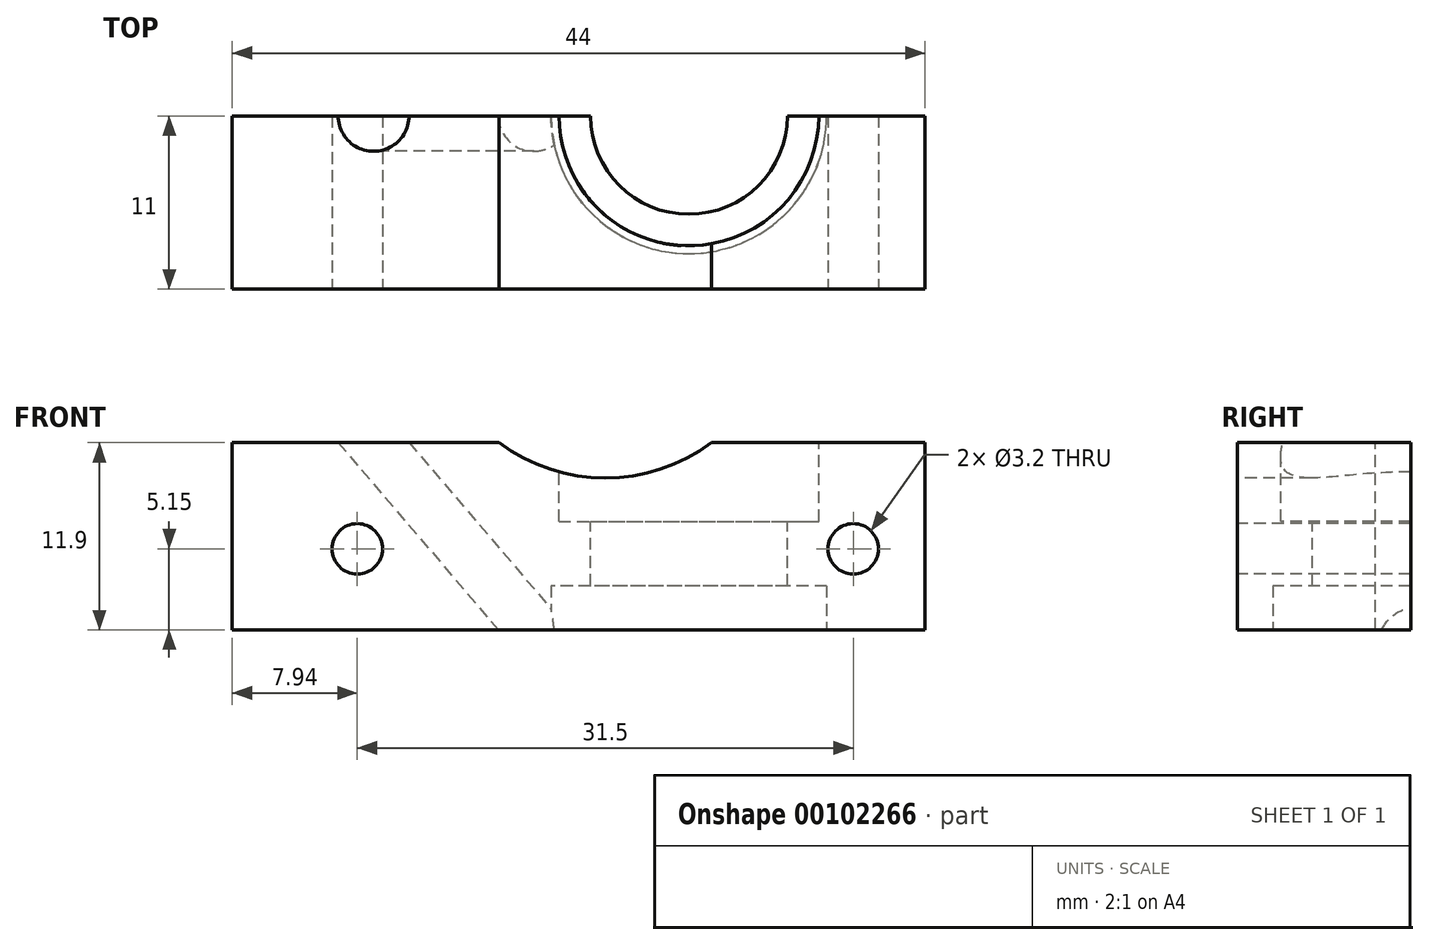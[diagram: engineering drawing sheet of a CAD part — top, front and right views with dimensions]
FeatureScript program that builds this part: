
annotation { "Feature Type Name" : "Feature", "Feature Type Description" : "" }
export const myFeature = defineFeature(function(context is Context, id is Id, definition is map)
    precondition{}
    {
        {
            var Q0;
            Q0=qCreatedBy(makeId("Top.planeOp"),FACE);
            var sketch = newSketch(context, id + "F0", { "sketchPlane" : qUnion([Q0])});
            skLineSegment(sketch, "E0.bottom", {"start": v(0, 0) * mm, "end": v(44, 0) * mm});
            skLineSegment(sketch, "E0.top", {"start": v(0, 11) * mm, "end": v(44, 11) * mm});
            skLineSegment(sketch, "E0.left", {"start": v(0, 0) * mm, "end": v(0, 11) * mm});
            skLineSegment(sketch, "E0.right", {"start": v(44, 0) * mm, "end": v(44, 11) * mm});
            skSolve(sketch);
        }
        {
            var Q0;
            Q0 = qSketchRegion(id + "F0", true);
            extrude(context, id + "F1", {"entities" : qUnion([Q0]), "depth" : 11.9 * mm});
        }
        {
            var Q0;
            Q0=makeQuery(id+"F1.opExtrude","CAP_FACE",FACE,{"disambiguationData":[OSD([sQuery(id+"F0.wireOp",EDGE,"E0.bottom"),sQuery(id+"F0.wireOp",EDGE,"E0.top"),sQuery(id+"F0.wireOp",EDGE,"E0.left"),sQuery(id+"F0.wireOp",EDGE,"E0.right")])],"isStart":false});
            var sketch = newSketch(context, id + "F2", { "sketchPlane" : qUnion([Q0])});
            skCircle(sketch, "E1", {"center": v(29, 11) * mm, "radius": 6.25 * mm});
            skSolve(sketch);
        }
        {
            var Q0;
            Q0 = qSketchRegion(id + "F2", true);
            extrude(context, id + "F3", {"entities" : qUnion([Q0]), "operationType" : NewBodyOperationType.REMOVE, "oppositeDirection" : true, "depth" : 25 * mm});
        }
        {
            var Q0;
            Q0=makeQuery(id+"F1.opExtrude","CAP_FACE",FACE,{"disambiguationData":[OSD([sQuery(id+"F0.wireOp",EDGE,"E0.bottom"),sQuery(id+"F0.wireOp",EDGE,"E0.top"),sQuery(id+"F0.wireOp",EDGE,"E0.left"),sQuery(id+"F0.wireOp",EDGE,"E0.right")])],"isStart":false});
            var sketch = newSketch(context, id + "F4", { "sketchPlane" : qUnion([Q0])});
            skCircle(sketch, "E2", {"center": v(29, 11) * mm, "radius": 8.25 * mm});
            skSolve(sketch);
        }
        {
            var Q0;
            Q0 = qSketchRegion(id + "F4", true);
            extrude(context, id + "F5", {"entities" : qUnion([Q0]), "operationType" : NewBodyOperationType.REMOVE, "oppositeDirection" : true, "depth" : 5 * mm});
        }
        {
            var Q0;
            Q0=makeQuery(id+"F1.opExtrude","CAP_FACE",FACE,{"disambiguationData":[OSD([sQuery(id+"F0.wireOp",EDGE,"E0.bottom"),sQuery(id+"F0.wireOp",EDGE,"E0.top"),sQuery(id+"F0.wireOp",EDGE,"E0.left"),sQuery(id+"F0.wireOp",EDGE,"E0.right")])],"isStart":true});
            var sketch = newSketch(context, id + "F6", { "sketchPlane" : qUnion([Q0])});
            skCircle(sketch, "E3", {"center": v(29, -11) * mm, "radius": 8.75 * mm});
            skSolve(sketch);
        }
        {
            var Q0;
            Q0 = qSketchRegion(id + "F6", true);
            extrude(context, id + "F7", {"entities" : qUnion([Q0]), "operationType" : NewBodyOperationType.REMOVE, "oppositeDirection" : true, "depth" : 2.8 * mm});
        }
        {
            var Q0;
            Q0=makeQuery(id+"F1.opExtrude","SWEPT_FACE",FACE,{"disambiguationData":[OSD([sQuery(id+"F0.wireOp",EDGE,"E0.bottom")])]});
            var sketch = newSketch(context, id + "F8", { "sketchPlane" : qUnion([Q0])});
            skCircle(sketch, "E4", {"center": v(39.44, 5.15) * mm, "radius": 1.6 * mm});
            skCircle(sketch, "E5", {"center": v(7.94, 5.15) * mm, "radius": 1.6 * mm});
            skCircle(sketch, "E6", {"center": v(23.7, 20.9) * mm, "radius": 11.25 * mm});
            skSolve(sketch);
        }
        {
            var Q0;
            Q0 = qSketchRegion(id + "F8", true);
            extrude(context, id + "F9", {"entities" : qUnion([Q0]), "operationType" : NewBodyOperationType.REMOVE, "oppositeDirection" : true, "depth" : 25 * mm});
        }
        {
            var Q0;
            {var subQ1=sQuery(id+"F0.wireOp",EDGE,"E0.left");var subQ2=sQuery(id+"F0.wireOp",EDGE,"E0.top");Q0=makeQuery(id+"F3.boolean.opBoolean","SPLIT",FACE,{"disambiguationData":[TD([makeQuery(id+"F1.opExtrude","SWEPT_FACE",FACE,{"disambiguationData":[OSD([subQ1])]})])],"derivedFrom":makeQuery(id+"F1.opExtrude","SWEPT_FACE",FACE,{"disambiguationData":[OSD([subQ2])]})});}
            var sketch = newSketch(context, id + "F10", { "sketchPlane" : qUnion([Q0])});
            skLineSegment(sketch, "E7", {"start": v(-22.5, -6.5) * mm, "end": v(-2.5, 16.9) * mm});
            skSolve(sketch);
        }
        {
            var Q0;
            Q0=makeQuery(id+"F1.opExtrude","CAP_FACE",FACE,{"disambiguationData":[OSD([sQuery(id+"F0.wireOp",EDGE,"E0.bottom"),sQuery(id+"F0.wireOp",EDGE,"E0.top"),sQuery(id+"F0.wireOp",EDGE,"E0.left"),sQuery(id+"F0.wireOp",EDGE,"E0.right")])],"isStart":true});
            var sketch = newSketch(context, id + "F11", { "sketchPlane" : qUnion([Q0])});
            skCircle(sketch, "E8", {"center": v(19.15, -11) * mm, "radius": 2.25 * mm});
            skSolve(sketch);
        }
        {
            var Q0;
            Q0 = qSketchRegion(id + "F11", true);
            var Q1;
            Q1=sQuery(id+"F10.wireOp",EDGE,"E7");
            sweep(context, id + "F12", {"operationType" : NewBodyOperationType.REMOVE, "profiles" : qUnion([Q0]), "path" : qUnion([Q1])});
        }
    });
